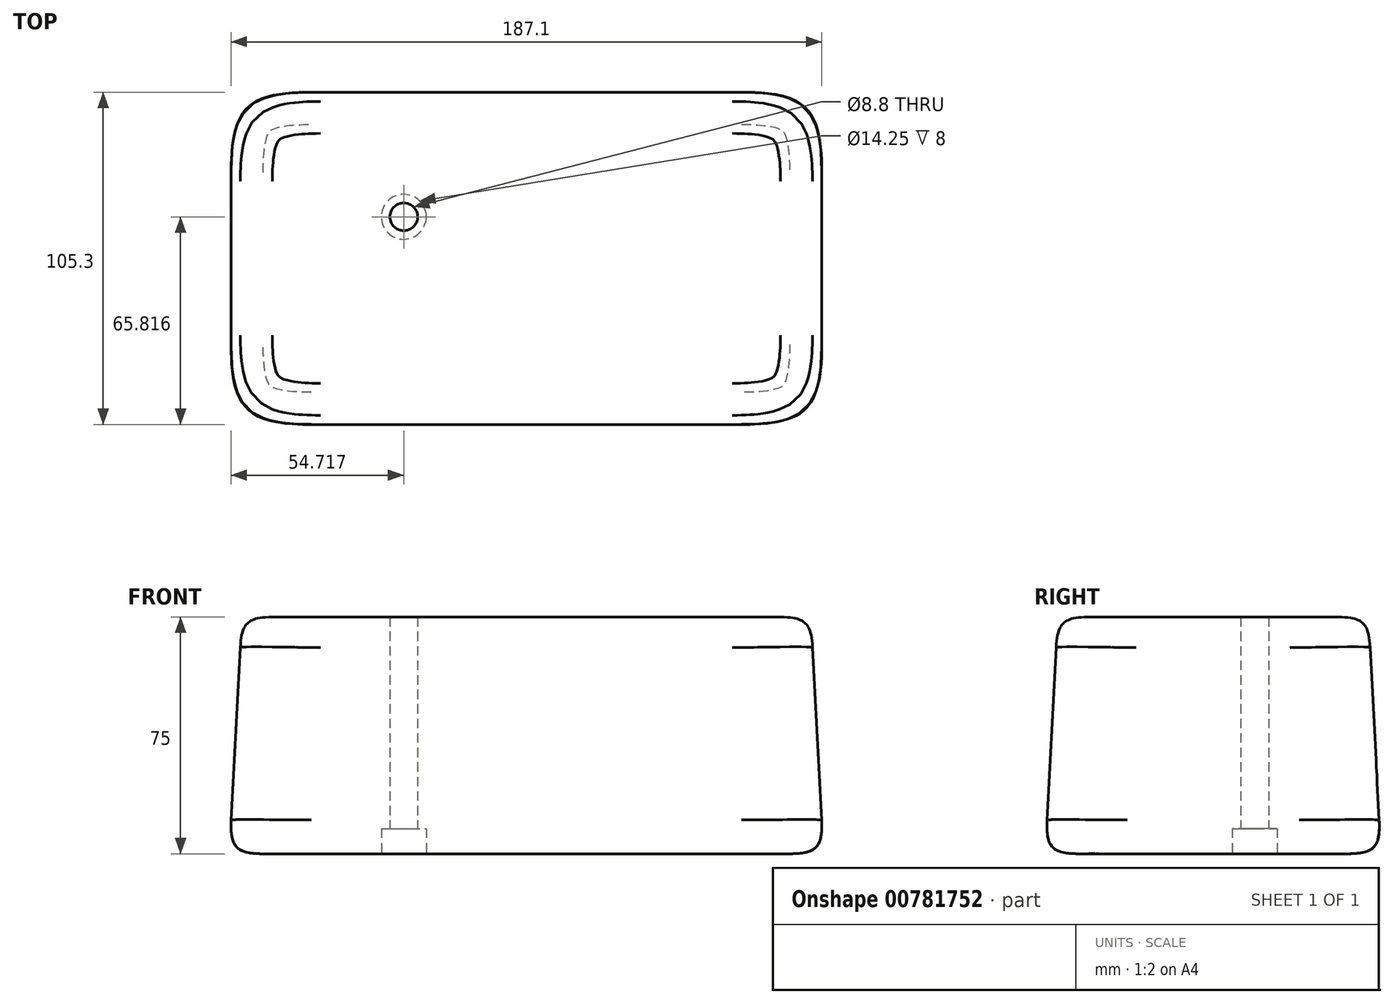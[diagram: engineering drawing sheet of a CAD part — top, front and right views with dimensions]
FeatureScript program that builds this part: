
annotation { "Feature Type Name" : "Feature", "Feature Type Description" : "" }
export const myFeature = defineFeature(function(context is Context, id is Id, definition is map)
    precondition{}
    {
        {
            var Q0;
            Q0=qCreatedBy(makeId("Top.planeOp"),FACE);
            var sketch = newSketch(context, id + "F0", { "sketchPlane" : qUnion([Q0])});
            skLineSegment(sketch, "E0.bottom", {"start": v(94.06, 53.16) * mm, "end": v(-94.06, 53.16) * mm});
            skLineSegment(sketch, "E0.top", {"start": v(94.06, -53.16) * mm, "end": v(-94.06, -53.16) * mm});
            skLineSegment(sketch, "E0.left", {"start": v(94.06, 53.16) * mm, "end": v(94.06, -53.16) * mm});
            skLineSegment(sketch, "E0.right", {"start": v(-94.06, 53.16) * mm, "end": v(-94.06, -53.16) * mm});
            skPoint(sketch, "E0.middle", {"position": v(0, 0) * mm});
            skSolve(sketch);
        }
        {
            var Q0;
            Q0=makeQuery(id+"F0.imprint","IMPRINT",FACE,{"disambiguationData":[TD([[makeQuery(id+"F0.imprint","IMPRINT",EDGE,{"derivedFrom":sQuery(id+"F0.wireOp",EDGE,"E0.bottom")}),1.0]])]});
            extrude(context, id + "F1", {"entities" : qUnion([Q0]), "depth" : 75 * mm, "offsetDistance" : 25.4 * mm, "hasDraft" : true, "draftAngle" : 3 * degree, "draftPullDirection" : true});
        }
        {
            var Q0;
            Q0=makeQuery(id+"F1.opExtrude","SWEPT_EDGE",EDGE,{"disambiguationData":[OSD([sQuery(id+"F0.wireOp",EDGE,"E0.bottom"),sQuery(id+"F0.wireOp",EDGE,"E0.right")])]});
            var Q1;
            Q1=makeQuery(id+"F1.opExtrude","SWEPT_EDGE",EDGE,{"disambiguationData":[OSD([sQuery(id+"F0.wireOp",EDGE,"E0.bottom"),sQuery(id+"F0.wireOp",EDGE,"E0.left")])]});
            var Q2;
            Q2=makeQuery(id+"F1.opExtrude","SWEPT_EDGE",EDGE,{"disambiguationData":[OSD([sQuery(id+"F0.wireOp",EDGE,"E0.top"),sQuery(id+"F0.wireOp",EDGE,"E0.right")])]});
            var Q3;
            Q3=makeQuery(id+"F1.opExtrude","SWEPT_EDGE",EDGE,{"disambiguationData":[OSD([sQuery(id+"F0.wireOp",EDGE,"E0.top"),sQuery(id+"F0.wireOp",EDGE,"E0.left")])]});
            fillet(context, id + "F2", {"entities" : qUnion([Q0, Q1, Q2, Q3]), "radius" : 25.4 * mm, "tangentPropagation" : true, "rho" : 0.6, "crossSection" : FilletCrossSection.CONIC, "allowEdgeOverflow" : false});
        }
        {
            var Q0;
            Q0=makeQuery(id+"F1.opExtrude","CAP_FACE",FACE,{"disambiguationData":[OSD([sQuery(id+"F0.wireOp",EDGE,"E0.bottom"),sQuery(id+"F0.wireOp",EDGE,"E0.top"),sQuery(id+"F0.wireOp",EDGE,"E0.left"),sQuery(id+"F0.wireOp",EDGE,"E0.right")])],"isStart":false});
            var Q1;
            Q1=makeQuery(id+"F1.opExtrude","CAP_FACE",FACE,{"disambiguationData":[OSD([sQuery(id+"F0.wireOp",EDGE,"E0.bottom"),sQuery(id+"F0.wireOp",EDGE,"E0.top"),sQuery(id+"F0.wireOp",EDGE,"E0.left"),sQuery(id+"F0.wireOp",EDGE,"E0.right")])],"isStart":true});
            fillet(context, id + "F3", {"entities" : qUnion([Q0, Q1]), "radius" : 10.16 * mm, "tangentPropagation" : true, "rho" : 0.6, "crossSection" : FilletCrossSection.CONIC, "allowEdgeOverflow" : false});
        }
        {
            var Q0;
            Q0=makeQuery(id+"F1.opExtrude","CAP_FACE",FACE,{"disambiguationData":[OSD([sQuery(id+"F0.wireOp",EDGE,"E0.bottom"),sQuery(id+"F0.wireOp",EDGE,"E0.top"),sQuery(id+"F0.wireOp",EDGE,"E0.left"),sQuery(id+"F0.wireOp",EDGE,"E0.right")])],"isStart":true});
            var sketch = newSketch(context, id + "F4", { "sketchPlane" : qUnion([Q0])});
            skPoint(sketch, "E1", {"position": v(-38.83, -13.17) * mm});
            skSolve(sketch);
        }
        {
            var Q0;
            Q0=sQuery(id+"F4.wireOp",VERTEX,"E1");
            var Q1;
            Q1=makeQuery(id+"F1.opExtrude","SWEPT_BODY",BODY,{"disambiguationData":[OSD([sQuery(id+"F0.wireOp",EDGE,"E0.bottom"),sQuery(id+"F0.wireOp",EDGE,"E0.top"),sQuery(id+"F0.wireOp",EDGE,"E0.left"),sQuery(id+"F0.wireOp",EDGE,"E0.right")])]});
            hole(context, id + "F5", {"style" : HoleStyle.C_BORE, "endStyle" : HoleEndStyle.THROUGH, "standardTappedOrClearance" : lookupTablePath({ "standard" : "ISO", "fit" : "Normal", "size" : "M8", "type" : "Clearance" }), "standardBlindInLast" : lookupTablePath({ "fit" : "Standard", "standard" : "ISO", "size" : "M8", "type" : "Clearance" }), "holeDiameter" : 8.8 * mm, "cBoreDiameter" : 14.25 * mm, "cBoreDepth" : 8 * mm, "majorDiameter" : 6.35 * mm, "isTappedThrough" : true, "tappedDepth" : 12.7 * mm, "tapClearance" : 3, "locations" : qUnion([Q0]), "scope" : qUnion([Q1])});
        }
    });
